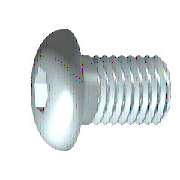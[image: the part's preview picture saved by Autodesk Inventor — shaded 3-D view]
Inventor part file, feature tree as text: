
AUTODESK INVENTOR PART (.ipt)
format: ipt  version: 2014 (Build 180170000, 170)  size: 194,048 bytes
history: native  units: mm (DEFAULTED — no unit token found)
features: sketch x2, extrude x1, plane x1, fillet x1
ambient origin geometry x7: Origin, YZ Plane, XY Plane, X Axis, Y Axis, Z Axis, Center Point
bodies: Solid1 (feature_tree), Body (feature_tree)
feature tree (5):
  extrude  "Slot"  Depth=2.5654mm
  plane  "Work Plane1"
  fillet  "Fillet2"  Radius=2.5654mm
  sketch  "Sketch1"  dims[d1=16.9416mm d2=2.1083mm d3=2.5654mm]
  sketch  "Sketch2"  dims[d4=1.778mm d5=60.0deg d6=4.826mm d7=4.826mm d8=3.666174mm d9=9.1694mm d10=90.0deg d11=10.0mm d12=0.0mm d13=16.9416mm d14=0.0mm d15=0.649224mm d16=0.649224mm d17=2.3114mm d19=0.0mm d26=19.05mm d27=45.0deg d28=0.0mm d29=0.0mm d30=0.1mm]
